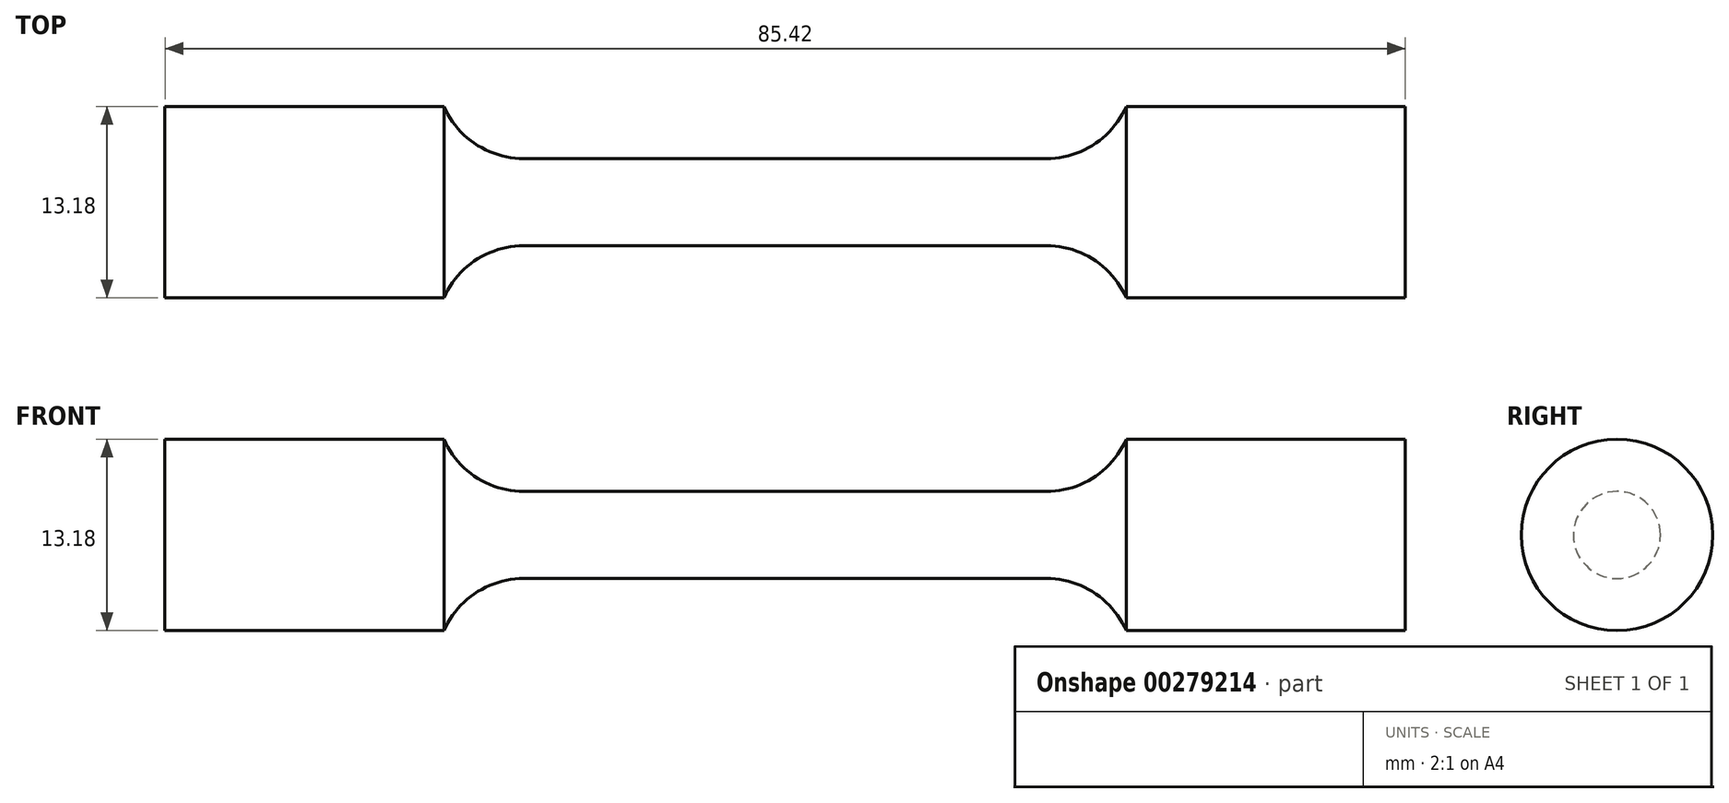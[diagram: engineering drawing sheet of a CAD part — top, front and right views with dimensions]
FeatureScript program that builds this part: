
annotation { "Feature Type Name" : "Feature", "Feature Type Description" : "" }
export const myFeature = defineFeature(function(context is Context, id is Id, definition is map)
    precondition{}
    {
        {
            var Q0;
            Q0=qCreatedBy(makeId("Front.planeOp"),FACE);
            var sketch = newSketch(context, id + "F0", { "sketchPlane" : qUnion([Q0])});
            skLineSegment(sketch, "E0", {"start": v(0, 3) * mm, "end": v(18, 3) * mm});
            skArc(sketch, "E1", {"start": v(18, 3) * mm, "mid": v(21.28, 3.98) * mm, "end": v(23.5, 6.6) * mm});
            skLineSegment(sketch, "E2", {"start": v(23.5, 6.6) * mm, "end": v(42.71, 6.6) * mm});
            skLineSegment(sketch, "E3", {"start": v(42.71, 6.6) * mm, "end": v(42.71, 0) * mm});
            skLineSegment(sketch, "E4.MirrorCS", {"start": v(0, 3) * mm, "end": v(-18, 3) * mm});
            skLineSegment(sketch, "E5.MirrorCS", {"start": v(-42.71, 6.6) * mm, "end": v(-42.71, 0) * mm});
            skLineSegment(sketch, "E6.MirrorCS", {"start": v(-23.5, 6.6) * mm, "end": v(-42.71, 6.6) * mm});
            skArc(sketch, "E7.MirrorCS", {"start": v(-18, 3) * mm, "mid": v(-21.28, 3.98) * mm, "end": v(-23.5, 6.6) * mm});
            skLineSegment(sketch, "E8", {"start": v(-42.71, 0) * mm, "end": v(42.71, 0) * mm});
            skSolve(sketch);
        }
        {
            var Q0;
            Q0 = qSketchRegion(id + "F0", true);
            var Q1;
            Q1=sQuery(id+"F0.wireOp",EDGE,"E8");
            revolve(context, id + "F1", {"entities" : qUnion([Q0]), "axis" : qUnion([Q1]), "revolveType" : RevolveType.FULL});
        }
    });
